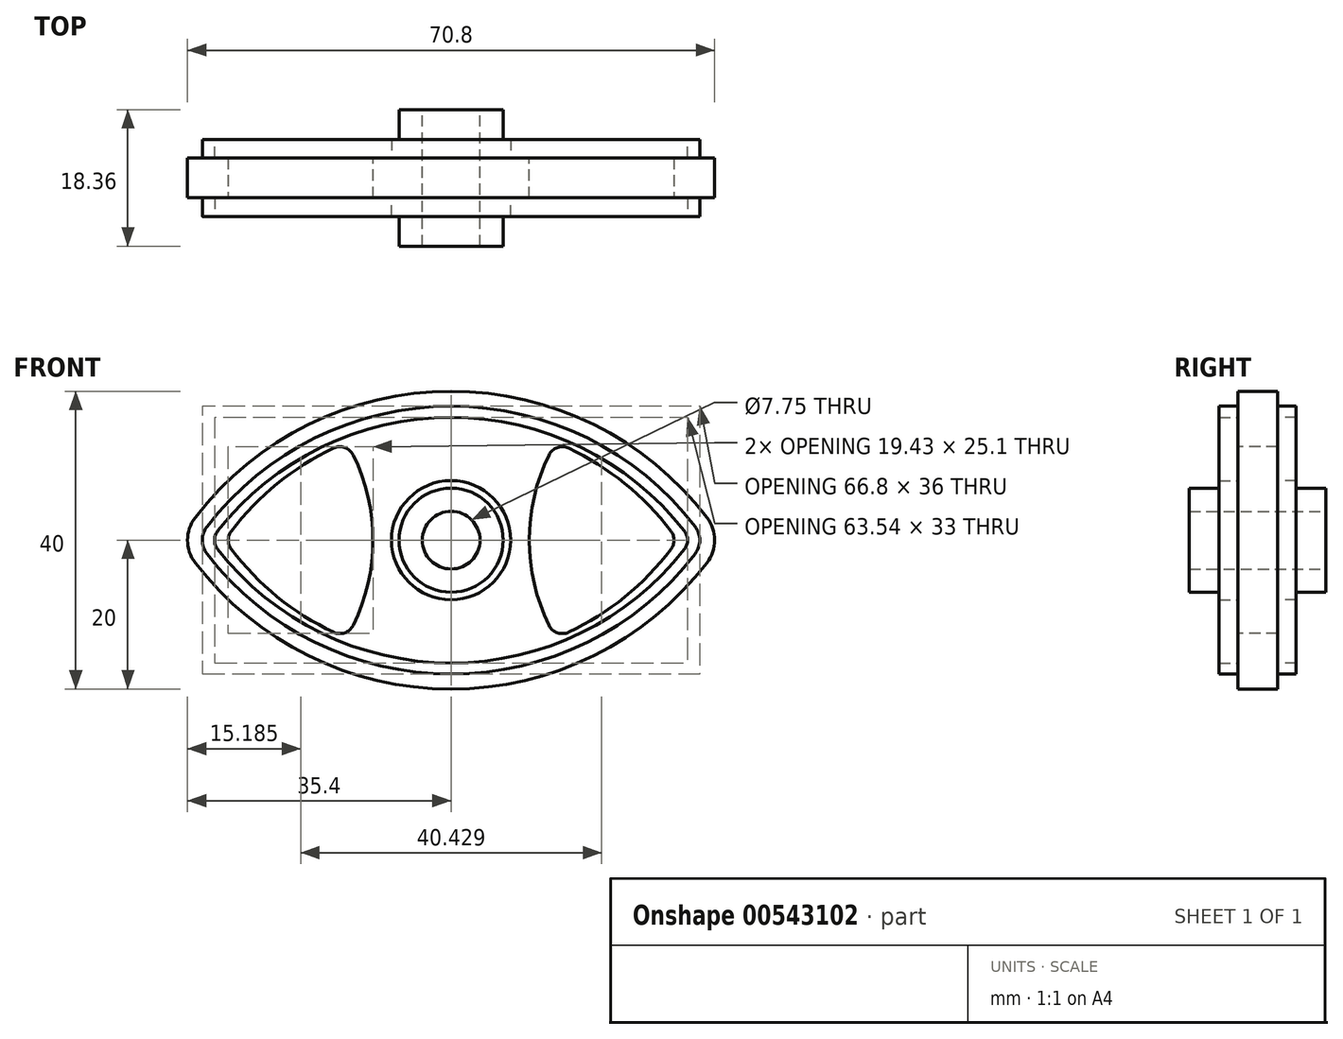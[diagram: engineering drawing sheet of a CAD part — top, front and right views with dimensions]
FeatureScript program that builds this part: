
annotation { "Feature Type Name" : "Feature", "Feature Type Description" : "" }
export const myFeature = defineFeature(function(context is Context, id is Id, definition is map)
    precondition{}
    {
        {
            var Q0;
            Q0=qCreatedBy(makeId("Front.planeOp"),FACE);
            var sketch = newSketch(context, id + "F0", { "sketchPlane" : qUnion([Q0])});
            skCircle(sketch, "E0", {"center": v(0, 0) * mm, "radius": 3.88 * mm});
            skLineSegment(sketch, "E1", {"start": v(-36.5, 0) * mm, "end": v(36.5, 0) * mm, "construction": true});
            skLineSegment(sketch, "E2", {"start": v(0, 20) * mm, "end": v(0, -20) * mm, "construction": true});
            skArc(sketch, "E3", {"start": v(34.37, 3.04) * mm, "mid": v(0, 20) * mm, "end": v(-34.37, 3.04) * mm});
            skArc(sketch, "E4.MirrorCS", {"start": v(34.37, -3.04) * mm, "mid": v(0, -20) * mm, "end": v(-34.37, -3.04) * mm});
            skPoint(sketch, "E5.visualSharp", {"position": v(-36.5, 0) * mm});
            skArc(sketch, "E5.filletArc", {"start": v(-34.37, 3.04) * mm, "mid": v(-35.4, 0) * mm, "end": v(-34.37, -3.04) * mm});
            skPoint(sketch, "E6.visualSharp", {"position": v(36.5, 0) * mm});
            skArc(sketch, "E6.filletArc", {"start": v(34.37, -3.04) * mm, "mid": v(35.4, 0) * mm, "end": v(34.37, 3.04) * mm});
            skArc(sketch, "E7", {"start": v(30.4, 0) * mm, "mid": v(23.18, 7.75) * mm, "end": v(14.06, 13.13) * mm});
            skArc(sketch, "E8.MirrorCS", {"start": v(30.4, 0) * mm, "mid": v(23.18, -7.75) * mm, "end": v(14.06, -13.13) * mm});
            skArc(sketch, "E9", {"start": v(14.06, 13.13) * mm, "mid": v(10.5, 0) * mm, "end": v(14.06, -13.13) * mm});
            skArc(sketch, "E10.MirrorCS", {"start": v(-14.06, 13.13) * mm, "mid": v(-10.5, 0) * mm, "end": v(-14.06, -13.13) * mm});
            skArc(sketch, "E11.MirrorCS", {"start": v(-30.4, 0) * mm, "mid": v(-23.18, 7.75) * mm, "end": v(-14.06, 13.13) * mm});
            skArc(sketch, "E12.MirrorCS", {"start": v(-30.4, 0) * mm, "mid": v(-23.18, -7.75) * mm, "end": v(-14.06, -13.13) * mm});
            skSolve(sketch);
        }
        {
            var Q0;
            Q0=makeQuery(id+"F0.imprint","IMPRINT",FACE,{"disambiguationData":[TD([[makeQuery(id+"F0.imprint","IMPRINT",EDGE,{"derivedFrom":sQuery(id+"F0.wireOp",EDGE,"E0")}),-1.0]])]});
            extrude(context, id + "F1", {"entities" : qUnion([Q0]), "endBound" : BoundingType.SYMMETRIC, "depth" : 5.35 * mm, "offsetDistance" : 25 * mm});
        }
        {
            var Q0;
            Q0=makeQuery(id+"F1.opExtrude","SWEPT_EDGE",EDGE,{"disambiguationData":[OSD([sQuery(id+"F0.wireOp",EDGE,"E10.MirrorCS"),sQuery(id+"F0.wireOp",EDGE,"E11.MirrorCS")])]});
            var Q1;
            Q1=makeQuery(id+"F1.opExtrude","SWEPT_EDGE",EDGE,{"disambiguationData":[OSD([sQuery(id+"F0.wireOp",EDGE,"E11.MirrorCS"),sQuery(id+"F0.wireOp",EDGE,"E12.MirrorCS")])]});
            var Q2;
            Q2=makeQuery(id+"F1.opExtrude","SWEPT_EDGE",EDGE,{"disambiguationData":[OSD([sQuery(id+"F0.wireOp",EDGE,"E10.MirrorCS"),sQuery(id+"F0.wireOp",EDGE,"E12.MirrorCS")])]});
            var Q3;
            Q3=makeQuery(id+"F1.opExtrude","SWEPT_EDGE",EDGE,{"disambiguationData":[OSD([sQuery(id+"F0.wireOp",EDGE,"E7"),sQuery(id+"F0.wireOp",EDGE,"E9")])]});
            var Q4;
            Q4=makeQuery(id+"F1.opExtrude","SWEPT_EDGE",EDGE,{"disambiguationData":[OSD([sQuery(id+"F0.wireOp",EDGE,"E7"),sQuery(id+"F0.wireOp",EDGE,"E8.MirrorCS")])]});
            var Q5;
            Q5=makeQuery(id+"F1.opExtrude","SWEPT_EDGE",EDGE,{"disambiguationData":[OSD([sQuery(id+"F0.wireOp",EDGE,"E8.MirrorCS"),sQuery(id+"F0.wireOp",EDGE,"E9")])]});
            fillet(context, id + "F2", {"entities" : qUnion([Q0, Q1, Q2, Q3, Q4, Q5]), "radius" : 2 * mm, "tangentPropagation" : true, "allowEdgeOverflow" : false});
        }
        {
            var Q0;
            Q0=makeQuery(id+"F1.opExtrude","CAP_FACE",FACE,{"disambiguationData":[OSD([sQuery(id+"F0.wireOp",EDGE,"E0"),sQuery(id+"F0.wireOp",EDGE,"E3"),sQuery(id+"F0.wireOp",EDGE,"E4.MirrorCS"),sQuery(id+"F0.wireOp",EDGE,"E5.filletArc"),sQuery(id+"F0.wireOp",EDGE,"E6.filletArc"),sQuery(id+"F0.wireOp",EDGE,"E7"),sQuery(id+"F0.wireOp",EDGE,"E8.MirrorCS"),sQuery(id+"F0.wireOp",EDGE,"E9"),sQuery(id+"F0.wireOp",EDGE,"E10.MirrorCS"),sQuery(id+"F0.wireOp",EDGE,"E11.MirrorCS"),sQuery(id+"F0.wireOp",EDGE,"E12.MirrorCS")])],"isStart":false});
            var sketch = newSketch(context, id + "F3", { "sketchPlane" : qUnion([Q0])});
            skArc(sketch, "E13.0", {"start": v(32.78, 1.83) * mm, "mid": v(0, 18) * mm, "end": v(-32.78, 1.83) * mm});
            skArc(sketch, "E13.1", {"start": v(32.78, -1.83) * mm, "mid": v(33.4, 0) * mm, "end": v(32.78, 1.83) * mm});
            skArc(sketch, "E13.2", {"start": v(32.78, -1.83) * mm, "mid": v(0, -18) * mm, "end": v(-32.78, -1.83) * mm});
            skArc(sketch, "E13.3", {"start": v(-32.78, 1.83) * mm, "mid": v(-33.4, 0) * mm, "end": v(-32.78, -1.83) * mm});
            skArc(sketch, "E14.0", {"start": v(32.27, 0) * mm, "mid": v(0, 16.5) * mm, "end": v(-32.27, 0) * mm});
            skArc(sketch, "E14.1", {"start": v(32.27, 0) * mm, "mid": v(0, -16.5) * mm, "end": v(-32.27, 0) * mm});
            skCircle(sketch, "E15", {"center": v(0, 0) * mm, "radius": 8 * mm});
            skSolve(sketch);
        }
        {
            var Q0;
            Q0=makeQuery(id+"F3.imprint","IMPRINT",FACE,{"disambiguationData":[TD([[makeQuery(id+"F3.imprint","IMPRINT",EDGE,{"derivedFrom":sQuery(id+"F3.wireOp",EDGE,"E13.0")}),1.0]])]});
            var Q1;
            Q1=makeQuery(id+"F3.imprint","IMPRINT",FACE,{"disambiguationData":[TD([[makeQuery(id+"F3.imprint","IMPRINT",EDGE,{"derivedFrom":sQuery(id+"F3.wireOp",EDGE,"E15")}),1.0]])]});
            extrude(context, id + "F4", {"entities" : qUnion([Q0, Q1]), "operationType" : NewBodyOperationType.ADD, "depth" : 2.5 * mm, "offsetDistance" : 25 * mm});
        }
        {
            var Q0;
            {var subQ0=sQuery(id+"F3.wireOp",EDGE,"E14.1");var subQ1=sQuery(id+"F3.wireOp",EDGE,"E14.0");Q0=makeQuery(id+"F4.opExtrude","SWEPT_EDGE",EDGE,{"disambiguationData":[OSD([subQ1,subQ0]),TDD([makeQuery(id+"F3.imprint","INTERSECT",VERTEX,{"disambiguationData":[OD(1.0)],"derivedFrom":[subQ1,subQ0]})])]});}
            var Q1;
            {var subQ0=sQuery(id+"F3.wireOp",EDGE,"E14.1");var subQ1=sQuery(id+"F3.wireOp",EDGE,"E14.0");Q1=makeQuery(id+"F4.opExtrude","SWEPT_EDGE",EDGE,{"disambiguationData":[OSD([subQ1,subQ0]),TDD([makeQuery(id+"F3.imprint","INTERSECT",VERTEX,{"disambiguationData":[OD(0.0)],"derivedFrom":[subQ1,subQ0]})])]});}
            fillet(context, id + "F5", {"entities" : qUnion([Q0, Q1]), "radius" : 2 * mm, "tangentPropagation" : true, "allowEdgeOverflow" : false});
        }
        {
            var Q0;
            Q0=makeQuery(id+"F4.opExtrude","CAP_FACE",FACE,{"disambiguationData":[OSD([sQuery(id+"F0.wireOp",EDGE,"E0"),sQuery(id+"F3.wireOp",EDGE,"E15")])],"isStart":false});
            var sketch = newSketch(context, id + "F6", { "sketchPlane" : qUnion([Q0])});
            skCircle(sketch, "E16", {"center": v(0, 0) * mm, "radius": 7 * mm});
            skSolve(sketch);
        }
        {
            var Q0;
            Q0=makeQuery(id+"F6.imprint","IMPRINT",FACE,{"disambiguationData":[TD([[makeQuery(id+"F6.imprint","IMPRINT",EDGE,{"derivedFrom":sQuery(id+"F6.wireOp",EDGE,"E16")}),1.0]])]});
            extrude(context, id + "F7", {"entities" : qUnion([Q0]), "operationType" : NewBodyOperationType.ADD, "depth" : 4 * mm, "offsetDistance" : 25 * mm});
        }
        {
            var Q0;
            Q0=makeQuery(id+"F1.opExtrude","SWEPT_BODY",BODY,{"disambiguationData":[OSD([sQuery(id+"F0.wireOp",EDGE,"E0"),sQuery(id+"F0.wireOp",EDGE,"E3"),sQuery(id+"F0.wireOp",EDGE,"E4.MirrorCS"),sQuery(id+"F0.wireOp",EDGE,"E5.filletArc"),sQuery(id+"F0.wireOp",EDGE,"E6.filletArc"),sQuery(id+"F0.wireOp",EDGE,"E7"),sQuery(id+"F0.wireOp",EDGE,"E8.MirrorCS"),sQuery(id+"F0.wireOp",EDGE,"E9"),sQuery(id+"F0.wireOp",EDGE,"E10.MirrorCS"),sQuery(id+"F0.wireOp",EDGE,"E11.MirrorCS"),sQuery(id+"F0.wireOp",EDGE,"E12.MirrorCS")])]});
            var Q1;
            Q1=qCreatedBy(makeId("Front.planeOp"),FACE);
            mirror(context, id + "F8", {"operationType" : NewBodyOperationType.ADD, "entities" : qUnion([Q0]), "mirrorPlane" : qUnion([Q1])});
        }
    });
